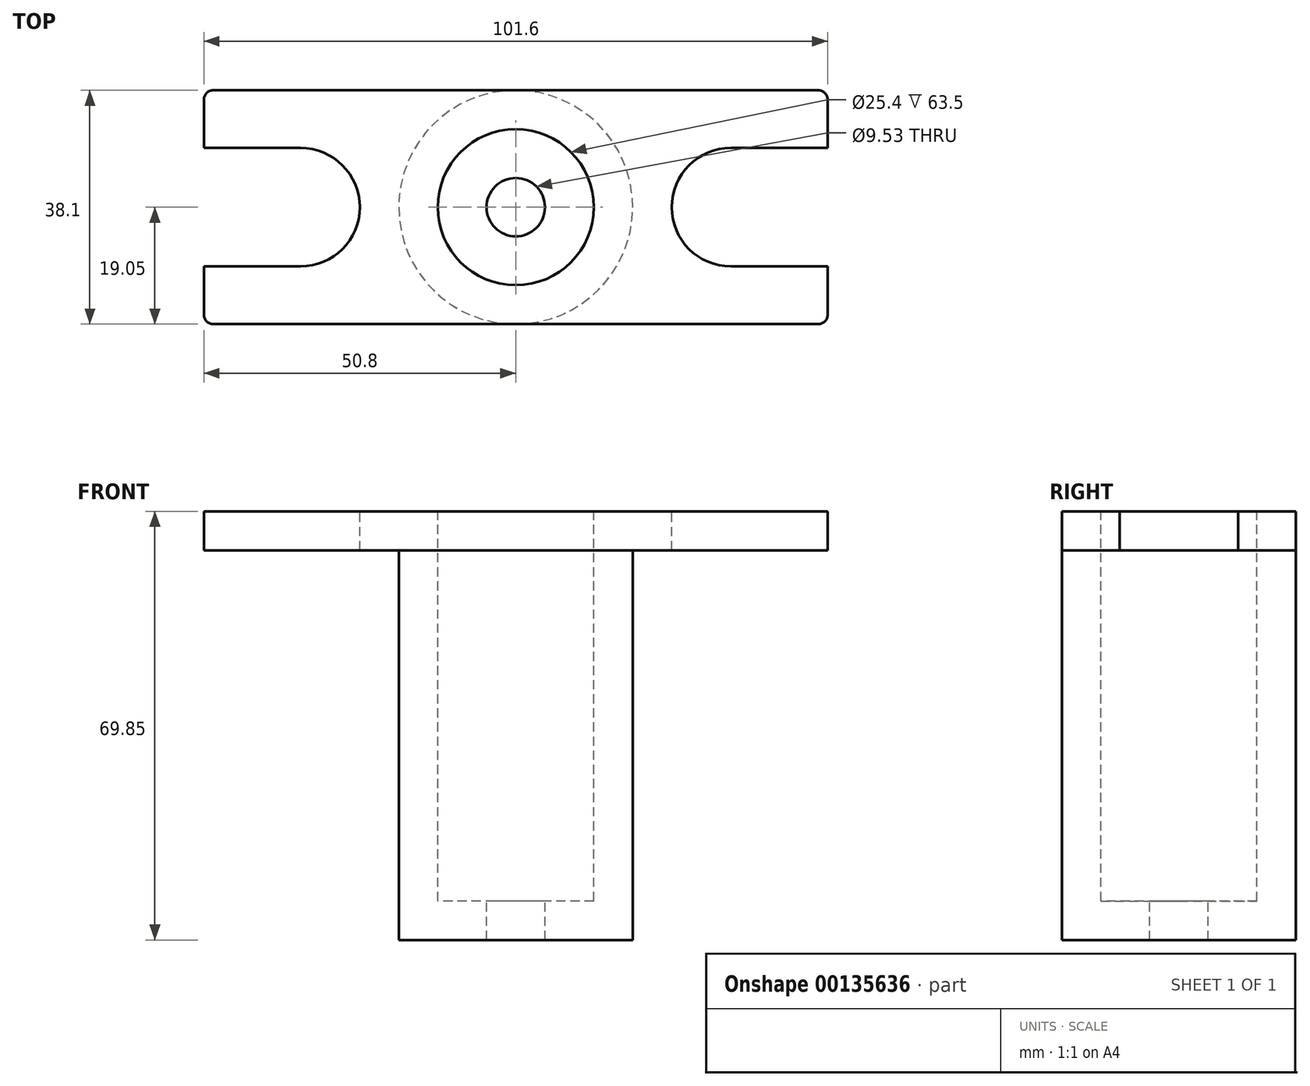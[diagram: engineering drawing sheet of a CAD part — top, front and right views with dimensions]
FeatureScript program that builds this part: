
annotation { "Feature Type Name" : "Feature", "Feature Type Description" : "" }
export const myFeature = defineFeature(function(context is Context, id is Id, definition is map)
    precondition{}
    {
        {
            var Q0;
            Q0=qCreatedBy(makeId("Front.planeOp"),FACE);
            var sketch = newSketch(context, id + "F0", { "sketchPlane" : qUnion([Q0])});
            skLineSegment(sketch, "E0.bottom", {"start": v(0, 0) * mm, "end": v(19.05, 0) * mm});
            skLineSegment(sketch, "E0.top", {"start": v(0, 63.5) * mm, "end": v(19.05, 63.5) * mm});
            skLineSegment(sketch, "E0.left", {"start": v(0, 0) * mm, "end": v(0, 63.5) * mm});
            skLineSegment(sketch, "E0.right", {"start": v(19.05, 0) * mm, "end": v(19.05, 63.5) * mm});
            skSolve(sketch);
        }
        {
            var Q0;
            Q0=makeQuery(id+"F0.imprint","IMPRINT",FACE,{"disambiguationData":[TD([[makeQuery(id+"F0.imprint","IMPRINT",EDGE,{"derivedFrom":sQuery(id+"F0.wireOp",EDGE,"E0.bottom")}),1.0]])]});
            var Q1;
            Q1=sQuery(id+"F0.wireOp",EDGE,"E0.left");
            revolve(context, id + "F1", {"entities" : qUnion([Q0]), "axis" : qUnion([Q1]), "revolveType" : RevolveType.FULL});
        }
        {
            var Q0;
            Q0=makeQuery(id+"F1.opRevolve","SWEPT_FACE",FACE,{"disambiguationData":[OSD([sQuery(id+"F0.wireOp",EDGE,"E0.top")])]});
            var sketch = newSketch(context, id + "F2", { "sketchPlane" : qUnion([Q0])});
            skLineSegment(sketch, "E1.bottom", {"start": v(-50.8, 19.05) * mm, "end": v(50.8, 19.05) * mm});
            skLineSegment(sketch, "E1.top", {"start": v(-50.8, -19.05) * mm, "end": v(50.8, -19.05) * mm});
            skLineSegment(sketch, "E1.left", {"start": v(-50.8, 19.05) * mm, "end": v(-50.8, -19.05) * mm});
            skLineSegment(sketch, "E1.right", {"start": v(50.8, 19.05) * mm, "end": v(50.8, -19.05) * mm});
            skSolve(sketch);
        }
        {
            var Q0;
            Q0 = qSketchRegion(id + "F2", true);
            extrude(context, id + "F3", {"entities" : qUnion([Q0]), "operationType" : NewBodyOperationType.ADD, "depth" : 6.35 * mm});
        }
        {
            var Q0;
            Q0=makeQuery(id+"F3.opExtrude","CAP_FACE",FACE,{"disambiguationData":[OSD([sQuery(id+"F2.wireOp",EDGE,"E1.bottom"),sQuery(id+"F2.wireOp",EDGE,"E1.top"),sQuery(id+"F2.wireOp",EDGE,"E1.left"),sQuery(id+"F2.wireOp",EDGE,"E1.right")])],"isStart":false});
            var sketch = newSketch(context, id + "F4", { "sketchPlane" : qUnion([Q0])});
            skCircle(sketch, "E2", {"center": v(0, 0) * mm, "radius": 12.7 * mm});
            skLineSegment(sketch, "E3", {"start": v(50.8, -9.65) * mm, "end": v(35.05, -9.65) * mm});
            skArc(sketch, "E4", {"start": v(35.05, 9.65) * mm, "mid": v(25.4, 0) * mm, "end": v(35.05, -9.65) * mm});
            skLineSegment(sketch, "E5", {"start": v(35.05, 9.65) * mm, "end": v(50.8, 9.65) * mm});
            skLineSegment(sketch, "E6", {"start": v(50.8, 9.65) * mm, "end": v(50.8, -9.65) * mm});
            skCircle(sketch, "E7", {"center": v(0, 0) * mm, "radius": 4.76 * mm});
            skLineSegment(sketch, "E8", {"start": v(-50.8, -9.65) * mm, "end": v(-35.05, -9.65) * mm});
            skArc(sketch, "E9", {"start": v(-35.05, -9.65) * mm, "mid": v(-25.4, 0) * mm, "end": v(-35.05, 9.65) * mm});
            skLineSegment(sketch, "E10", {"start": v(-35.05, 9.65) * mm, "end": v(-50.8, 9.65) * mm});
            skSolve(sketch);
        }
        {
            var Q0;
            Q0=makeQuery(id+"F4.imprint","IMPRINT",FACE,{"disambiguationData":[TD([[makeQuery(id+"F4.imprint","IMPRINT",EDGE,{"derivedFrom":sQuery(id+"F4.wireOp",EDGE,"E3")}),-1.0]])]});
            extrude(context, id + "F5", {"entities" : qUnion([Q0]), "operationType" : NewBodyOperationType.REMOVE, "endBound" : BoundingType.UP_TO_NEXT, "oppositeDirection" : true, "depth" : 25.4 * mm});
        }
        {
            var Q0;
            Q0=makeQuery(id+"F4.imprint","IMPRINT",FACE,{"disambiguationData":[TD([[makeQuery(id+"F4.imprint","IMPRINT",EDGE,{"derivedFrom":sQuery(id+"F4.wireOp",EDGE,"E2")}),1.0]])]});
            extrude(context, id + "F6", {"entities" : qUnion([Q0]), "operationType" : NewBodyOperationType.REMOVE, "oppositeDirection" : true, "depth" : 63.5 * mm});
        }
        {
            var Q0;
            Q0=makeQuery(id+"F4.imprint","IMPRINT",FACE,{"disambiguationData":[TD([[makeQuery(id+"F4.imprint","IMPRINT",EDGE,{"derivedFrom":sQuery(id+"F4.wireOp",EDGE,"E7")}),1.0]])]});
            extrude(context, id + "F7", {"entities" : qUnion([Q0]), "operationType" : NewBodyOperationType.REMOVE, "endBound" : BoundingType.THROUGH_ALL, "oppositeDirection" : true, "depth" : 25.4 * mm});
        }
        {
            var Q0;
            {var subQ0=sQuery(id+"F4.wireOp",EDGE,"E8");Q0=makeQuery(id+"F4.imprint","IMPRINT",FACE,{"disambiguationData":[TD([[makeQuery(id+"F4.imprint","IMPRINT",EDGE,{"derivedFrom":subQ0}),1.0]])]});}
            extrude(context, id + "F8", {"entities" : qUnion([Q0]), "operationType" : NewBodyOperationType.REMOVE, "endBound" : BoundingType.UP_TO_NEXT, "oppositeDirection" : true, "depth" : 25.4 * mm});
        }
        {
            var Q0;
            Q0=makeQuery(id+"F3.opExtrude","SWEPT_EDGE",EDGE,{"disambiguationData":[OSD([sQuery(id+"F2.wireOp",EDGE,"E1.top"),sQuery(id+"F2.wireOp",EDGE,"E1.right")])]});
            var Q1;
            Q1=makeQuery(id+"F3.opExtrude","SWEPT_EDGE",EDGE,{"disambiguationData":[OSD([sQuery(id+"F2.wireOp",EDGE,"E1.bottom"),sQuery(id+"F2.wireOp",EDGE,"E1.right")])]});
            var Q2;
            Q2=makeQuery(id+"F3.opExtrude","SWEPT_EDGE",EDGE,{"disambiguationData":[OSD([sQuery(id+"F2.wireOp",EDGE,"E1.top"),sQuery(id+"F2.wireOp",EDGE,"E1.left")])]});
            var Q3;
            Q3=makeQuery(id+"F3.opExtrude","SWEPT_EDGE",EDGE,{"disambiguationData":[OSD([sQuery(id+"F2.wireOp",EDGE,"E1.bottom"),sQuery(id+"F2.wireOp",EDGE,"E1.left")])]});
            fillet(context, id + "F9", {"entities" : qUnion([Q0, Q1, Q2, Q3]), "radius" : 1.52 * mm, "tangentPropagation" : true, "allowEdgeOverflow" : false});
        }
    });
